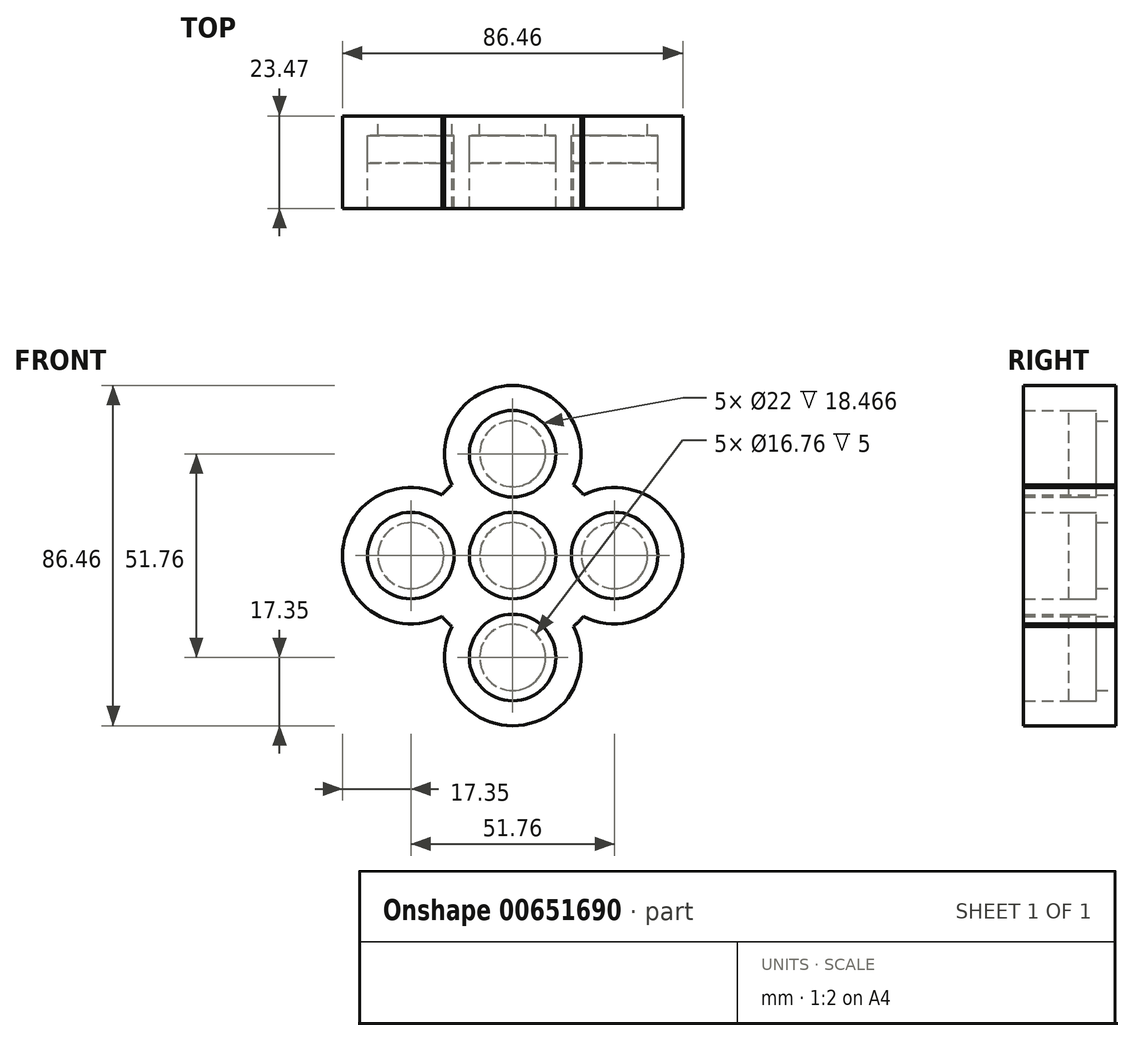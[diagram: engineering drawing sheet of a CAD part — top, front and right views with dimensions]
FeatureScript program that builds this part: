
annotation { "Feature Type Name" : "Feature", "Feature Type Description" : "" }
export const myFeature = defineFeature(function(context is Context, id is Id, definition is map)
    precondition{}
    {
        {
            var Q0;
            Q0=qCreatedBy(makeId("Front.planeOp"),FACE);
            var sketch = newSketch(context, id + "F0", { "sketchPlane" : qUnion([Q0])});
            skCircle(sketch, "E0", {"center": v(0, 0) * mm, "radius": 11 * mm});
            skCircle(sketch, "E1", {"center": v(-25.88, 0) * mm, "radius": 11 * mm});
            skCircle(sketch, "E2", {"center": v(25.88, 0) * mm, "radius": 11 * mm});
            skCircle(sketch, "E3", {"center": v(0, -25.88) * mm, "radius": 11 * mm});
            skCircle(sketch, "E4", {"center": v(0, 25.88) * mm, "radius": 11 * mm});
            skArc(sketch, "E5.0", {"start": v(15.45, 17.98) * mm, "mid": v(0, 43.23) * mm, "end": v(-15.45, 17.98) * mm});
            skArc(sketch, "E6.0", {"start": v(17.98, 15.45) * mm, "mid": v(16.76, 16.76) * mm, "end": v(15.45, 17.98) * mm});
            skArc(sketch, "E7.0", {"start": v(17.98, -15.45) * mm, "mid": v(43.23, 0) * mm, "end": v(17.98, 15.45) * mm});
            skArc(sketch, "E8.0", {"start": v(-15.45, -17.98) * mm, "mid": v(0, -43.23) * mm, "end": v(15.45, -17.98) * mm});
            skArc(sketch, "E9.0", {"start": v(-17.98, 15.45) * mm, "mid": v(-43.23, 0) * mm, "end": v(-17.98, -15.45) * mm});
            skArc(sketch, "E10.trimOffspring", {"start": v(-15.45, 17.98) * mm, "mid": v(-16.76, 16.76) * mm, "end": v(-17.98, 15.45) * mm});
            skArc(sketch, "E11.trimOffspring", {"start": v(-17.98, -15.45) * mm, "mid": v(-16.76, -16.76) * mm, "end": v(-15.45, -17.98) * mm});
            skArc(sketch, "E12.trimOffspring", {"start": v(15.45, -17.98) * mm, "mid": v(16.76, -16.76) * mm, "end": v(17.98, -15.45) * mm});
            skSolve(sketch);
        }
        {
            var Q0;
            Q0=makeQuery(id+"F0.imprint","IMPRINT",FACE,{"disambiguationData":[TD([[makeQuery(id+"F0.imprint","IMPRINT",EDGE,{"derivedFrom":sQuery(id+"F0.wireOp",EDGE,"E0")}),-1.0]])]});
            extrude(context, id + "F1", {"entities" : qUnion([Q0]), "depth" : 18.47 * mm, "offsetDistance" : 25.4 * mm});
        }
        {
            var Q0;
            Q0=makeQuery(id+"F0.imprint","IMPRINT",FACE,{"disambiguationData":[TD([[makeQuery(id+"F0.imprint","IMPRINT",EDGE,{"derivedFrom":sQuery(id+"F0.wireOp",EDGE,"E0")}),-1.0]])]});
            var Q1;
            Q1=makeQuery(id+"F0.imprint","IMPRINT",FACE,{"disambiguationData":[TD([[makeQuery(id+"F0.imprint","IMPRINT",EDGE,{"derivedFrom":sQuery(id+"F0.wireOp",EDGE,"E4")}),1.0]])]});
            var Q2;
            Q2=makeQuery(id+"F0.imprint","IMPRINT",FACE,{"disambiguationData":[TD([[makeQuery(id+"F0.imprint","IMPRINT",EDGE,{"derivedFrom":sQuery(id+"F0.wireOp",EDGE,"E2")}),1.0]])]});
            var Q3;
            Q3=makeQuery(id+"F0.imprint","IMPRINT",FACE,{"disambiguationData":[TD([[makeQuery(id+"F0.imprint","IMPRINT",EDGE,{"derivedFrom":sQuery(id+"F0.wireOp",EDGE,"E0")}),1.0]])]});
            var Q4;
            Q4=makeQuery(id+"F0.imprint","IMPRINT",FACE,{"disambiguationData":[TD([[makeQuery(id+"F0.imprint","IMPRINT",EDGE,{"derivedFrom":sQuery(id+"F0.wireOp",EDGE,"E1")}),1.0]])]});
            var Q5;
            Q5=makeQuery(id+"F0.imprint","IMPRINT",FACE,{"disambiguationData":[TD([[makeQuery(id+"F0.imprint","IMPRINT",EDGE,{"derivedFrom":sQuery(id+"F0.wireOp",EDGE,"E3")}),1.0]])]});
            extrude(context, id + "F2", {"entities" : qUnion([Q0, Q1, Q2, Q3, Q4, Q5]), "operationType" : NewBodyOperationType.ADD, "oppositeDirection" : true, "depth" : 5 * mm, "offsetDistance" : 25.4 * mm});
        }
        {
            var Q0;
            Q0=makeQuery(id+"F2.opExtrude","CAP_FACE",FACE,{"disambiguationData":[OSD([sQuery(id+"F0.wireOp",EDGE,"E5.0"),sQuery(id+"F0.wireOp",EDGE,"E6.0"),sQuery(id+"F0.wireOp",EDGE,"E7.0"),sQuery(id+"F0.wireOp",EDGE,"E8.0"),sQuery(id+"F0.wireOp",EDGE,"E9.0"),sQuery(id+"F0.wireOp",EDGE,"E10.trimOffspring"),sQuery(id+"F0.wireOp",EDGE,"E11.trimOffspring"),sQuery(id+"F0.wireOp",EDGE,"E12.trimOffspring")])],"isStart":false});
            var sketch = newSketch(context, id + "F3", { "sketchPlane" : qUnion([Q0])});
            skCircle(sketch, "E13", {"center": v(0, 25.88) * mm, "radius": 8.38 * mm});
            skCircle(sketch, "E14", {"center": v(-25.88, 0) * mm, "radius": 8.38 * mm});
            skCircle(sketch, "E15", {"center": v(0, 0) * mm, "radius": 8.38 * mm});
            skCircle(sketch, "E16", {"center": v(25.88, 0) * mm, "radius": 8.38 * mm});
            skCircle(sketch, "E17", {"center": v(0, -25.88) * mm, "radius": 8.38 * mm});
            skSolve(sketch);
        }
        {
            var Q0;
            Q0=makeQuery(id+"F3.imprint","IMPRINT",FACE,{"disambiguationData":[TD([[makeQuery(id+"F3.imprint","IMPRINT",EDGE,{"derivedFrom":sQuery(id+"F3.wireOp",EDGE,"E13")}),1.0]])]});
            var Q1;
            Q1=makeQuery(id+"F3.imprint","IMPRINT",FACE,{"disambiguationData":[TD([[makeQuery(id+"F3.imprint","IMPRINT",EDGE,{"derivedFrom":sQuery(id+"F3.wireOp",EDGE,"E14")}),1.0]])]});
            var Q2;
            Q2=makeQuery(id+"F3.imprint","IMPRINT",FACE,{"disambiguationData":[TD([[makeQuery(id+"F3.imprint","IMPRINT",EDGE,{"derivedFrom":sQuery(id+"F3.wireOp",EDGE,"E15")}),1.0]])]});
            var Q3;
            Q3=makeQuery(id+"F3.imprint","IMPRINT",FACE,{"disambiguationData":[TD([[makeQuery(id+"F3.imprint","IMPRINT",EDGE,{"derivedFrom":sQuery(id+"F3.wireOp",EDGE,"E17")}),1.0]])]});
            var Q4;
            Q4=makeQuery(id+"F3.imprint","IMPRINT",FACE,{"disambiguationData":[TD([[makeQuery(id+"F3.imprint","IMPRINT",EDGE,{"derivedFrom":sQuery(id+"F3.wireOp",EDGE,"E16")}),1.0]])]});
            extrude(context, id + "F4", {"entities" : qUnion([Q0, Q1, Q2, Q3, Q4]), "operationType" : NewBodyOperationType.REMOVE, "oppositeDirection" : true, "depth" : 25.4 * mm, "offsetDistance" : 25.4 * mm});
        }
        {
            var Q0;
            Q0=makeQuery(id+"F0.imprint","IMPRINT",FACE,{"disambiguationData":[TD([[makeQuery(id+"F0.imprint","IMPRINT",EDGE,{"derivedFrom":sQuery(id+"F0.wireOp",EDGE,"E4")}),1.0]])]});
            var Q1;
            Q1=makeQuery(id+"F0.imprint","IMPRINT",FACE,{"disambiguationData":[TD([[makeQuery(id+"F0.imprint","IMPRINT",EDGE,{"derivedFrom":sQuery(id+"F0.wireOp",EDGE,"E1")}),1.0]])]});
            var Q2;
            Q2=makeQuery(id+"F0.imprint","IMPRINT",FACE,{"disambiguationData":[TD([[makeQuery(id+"F0.imprint","IMPRINT",EDGE,{"derivedFrom":sQuery(id+"F0.wireOp",EDGE,"E0")}),1.0]])]});
            var Q3;
            Q3=makeQuery(id+"F0.imprint","IMPRINT",FACE,{"disambiguationData":[TD([[makeQuery(id+"F0.imprint","IMPRINT",EDGE,{"derivedFrom":sQuery(id+"F0.wireOp",EDGE,"E3")}),1.0]])]});
            var Q4;
            Q4=makeQuery(id+"F0.imprint","IMPRINT",FACE,{"disambiguationData":[TD([[makeQuery(id+"F0.imprint","IMPRINT",EDGE,{"derivedFrom":sQuery(id+"F0.wireOp",EDGE,"E2")}),1.0]])]});
            extrude(context, id + "F5", {"entities" : qUnion([Q0, Q1, Q2, Q3, Q4]), "depth" : 6.9 * mm, "offsetDistance" : 25.4 * mm});
        }
    });
